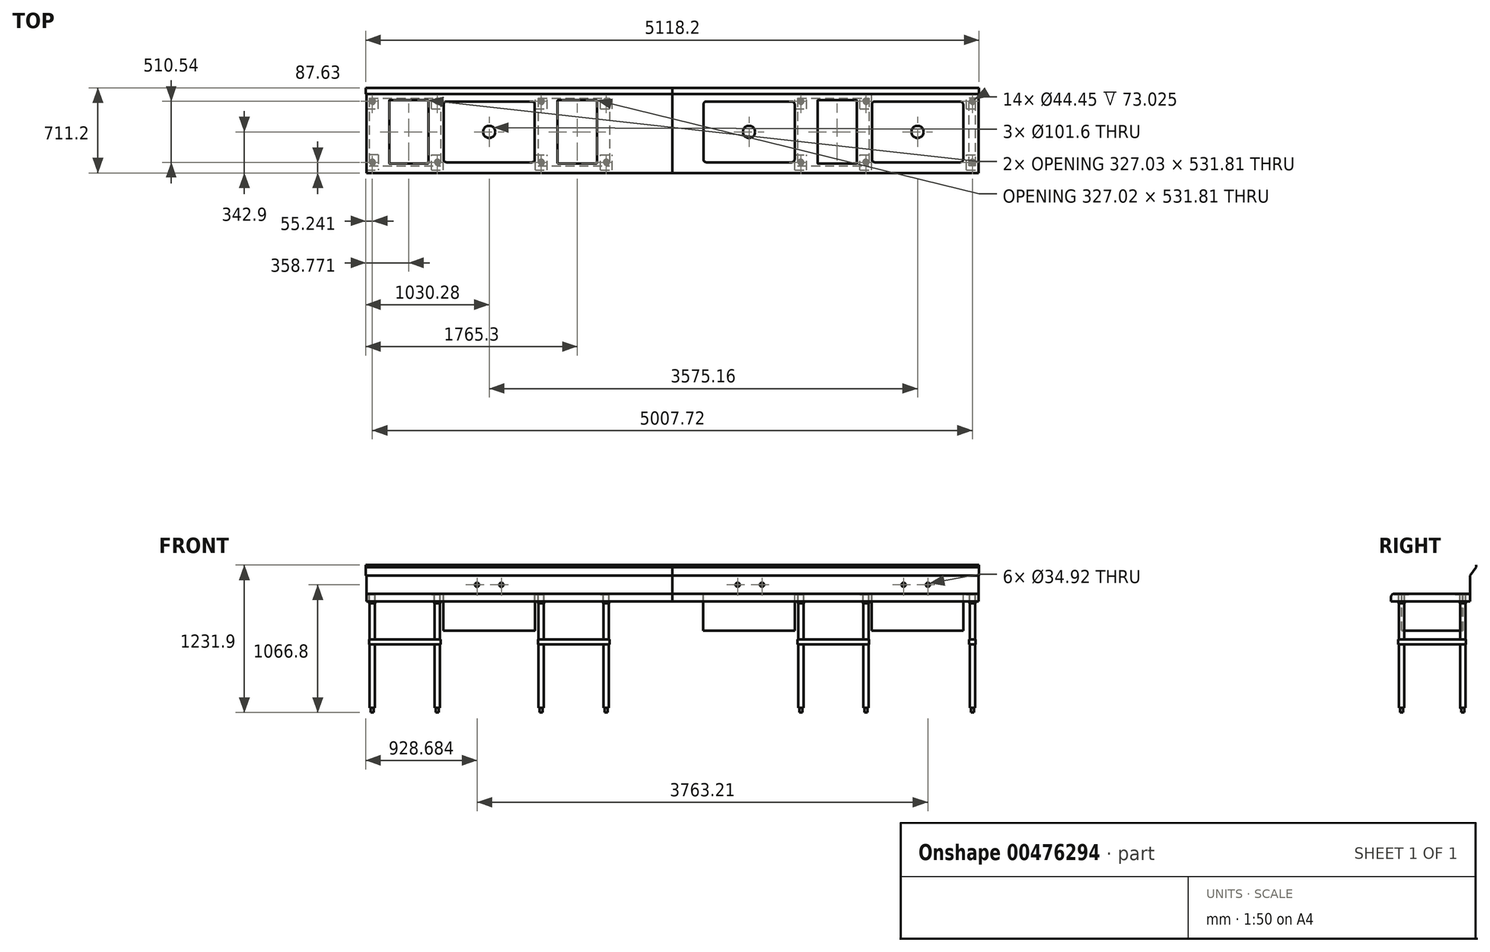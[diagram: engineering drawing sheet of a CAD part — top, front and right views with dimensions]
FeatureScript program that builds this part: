
annotation { "Feature Type Name" : "Feature", "Feature Type Description" : "" }
export const myFeature = defineFeature(function(context is Context, id is Id, definition is map)
    precondition{}
    {
        {
            var Q0;
            Q0=qCreatedBy(makeId("Top.planeOp"),FACE);
            var sketch = newSketch(context, id + "F0", { "sketchPlane" : qUnion([Q0])});
            skLineSegment(sketch, "E0.bottom", {"start": v(-2554.34, 342.9) * mm, "end": v(2554.34, 342.9) * mm});
            skLineSegment(sketch, "E0.top", {"start": v(-2554.34, -342.9) * mm, "end": v(2554.34, -342.9) * mm});
            skLineSegment(sketch, "E0.left", {"start": v(-2554.34, 342.9) * mm, "end": v(-2554.34, -342.9) * mm});
            skLineSegment(sketch, "E0.right", {"start": v(2554.34, 342.9) * mm, "end": v(2554.34, -342.9) * mm});
            skLineSegment(sketch, "E1", {"start": v(-2554.34, 0) * mm, "end": v(2554.34, 0) * mm, "construction": true});
            skLineSegment(sketch, "E2.bottom", {"start": v(-2363.84, 265.9) * mm, "end": v(-2036.82, 265.9) * mm, "construction": true});
            skLineSegment(sketch, "E2.top", {"start": v(-2363.84, -265.9) * mm, "end": v(-2036.82, -265.9) * mm, "construction": true});
            skLineSegment(sketch, "E2.left", {"start": v(-2363.84, 265.9) * mm, "end": v(-2363.84, -265.9) * mm, "construction": true});
            skLineSegment(sketch, "E2.right", {"start": v(-2036.82, 265.9) * mm, "end": v(-2036.82, -265.9) * mm, "construction": true});
            skLineSegment(sketch, "E3.bottom", {"start": v(-1909.82, 254) * mm, "end": v(-1147.82, 254) * mm, "construction": true});
            skLineSegment(sketch, "E3.top", {"start": v(-1909.82, -254) * mm, "end": v(-1147.82, -254) * mm, "construction": true});
            skLineSegment(sketch, "E3.left", {"start": v(-1909.82, 254) * mm, "end": v(-1909.82, -254) * mm, "construction": true});
            skLineSegment(sketch, "E3.right", {"start": v(-1147.82, 254) * mm, "end": v(-1147.82, -254) * mm, "construction": true});
            skLineSegment(sketch, "E4.bottom", {"start": v(-957.32, 265.9) * mm, "end": v(-630.3, 265.9) * mm, "construction": true});
            skLineSegment(sketch, "E4.top", {"start": v(-957.32, -265.9) * mm, "end": v(-630.3, -265.9) * mm, "construction": true});
            skLineSegment(sketch, "E4.left", {"start": v(-957.32, 265.9) * mm, "end": v(-957.32, -265.9) * mm, "construction": true});
            skLineSegment(sketch, "E4.right", {"start": v(-630.3, 265.9) * mm, "end": v(-630.3, -265.9) * mm, "construction": true});
            skLineSegment(sketch, "E5.bottom", {"start": v(258.82, 254) * mm, "end": v(1020.82, 254) * mm, "construction": true});
            skLineSegment(sketch, "E5.top", {"start": v(258.82, -254) * mm, "end": v(1020.82, -254) * mm, "construction": true});
            skLineSegment(sketch, "E5.left", {"start": v(258.82, 254) * mm, "end": v(258.82, -254) * mm, "construction": true});
            skLineSegment(sketch, "E5.right", {"start": v(1020.82, 254) * mm, "end": v(1020.82, -254) * mm, "construction": true});
            skLineSegment(sketch, "E6.bottom", {"start": v(1211.32, 265.9) * mm, "end": v(1538.34, 265.9) * mm, "construction": true});
            skLineSegment(sketch, "E6.top", {"start": v(1211.32, -265.9) * mm, "end": v(1538.34, -265.9) * mm, "construction": true});
            skLineSegment(sketch, "E6.left", {"start": v(1211.32, 265.9) * mm, "end": v(1211.32, -265.9) * mm, "construction": true});
            skLineSegment(sketch, "E6.right", {"start": v(1538.34, 265.9) * mm, "end": v(1538.34, -265.9) * mm, "construction": true});
            skLineSegment(sketch, "E7.bottom", {"start": v(1665.34, 254) * mm, "end": v(2427.34, 254) * mm, "construction": true});
            skLineSegment(sketch, "E7.top", {"start": v(1665.34, -254) * mm, "end": v(2427.34, -254) * mm, "construction": true});
            skLineSegment(sketch, "E7.left", {"start": v(1665.34, 254) * mm, "end": v(1665.34, -254) * mm, "construction": true});
            skLineSegment(sketch, "E7.right", {"start": v(2427.34, 254) * mm, "end": v(2427.34, -254) * mm, "construction": true});
            skLineSegment(sketch, "E8", {"start": v(-827.14, 342.9) * mm, "end": v(-827.14, -342.9) * mm, "construction": true});
            skLineSegment(sketch, "E9", {"start": v(900.06, 342.9) * mm, "end": v(900.06, -342.9) * mm, "construction": true});
            skLineSegment(sketch, "E10", {"start": v(-1528.82, 254) * mm, "end": v(-1528.82, -254) * mm, "construction": true});
            skPoint(sketch, "E11", {"position": v(-1528.82, 0) * mm});
            skPoint(sketch, "E12", {"position": v(-2363.84, 0) * mm});
            skSolve(sketch);
        }
        {
            var Q0;
            Q0 = qSketchRegion(id + "F0", true);
            extrude(context, id + "F1", {"entities" : qUnion([Q0]), "oppositeDirection" : true, "depth" : 304.93 * mm, "offsetDistance" : 25.4 * mm});
        }
        {
            var Q0;
            Q0=makeQuery(id+"F0.imprint","IMPRINT",FACE,{"disambiguationData":[TD([[makeQuery(id+"F0.imprint","IMPRINT",EDGE,{"derivedFrom":sQuery(id+"F0.wireOp",EDGE,"E0.bottom")}),-1.0]])]});
            var sketch = newSketch(context, id + "F2", { "sketchPlane" : qUnion([Q0])});
            skLineSegment(sketch, "E13.bottom", {"start": v(-1884.42, 254) * mm, "end": v(-1173.22, 254) * mm});
            skLineSegment(sketch, "E13.top", {"start": v(-1884.42, -254) * mm, "end": v(-1173.22, -254) * mm});
            skLineSegment(sketch, "E13.left", {"start": v(-1909.82, 228.6) * mm, "end": v(-1909.82, -228.6) * mm});
            skLineSegment(sketch, "E13.right", {"start": v(-1147.82, 228.6) * mm, "end": v(-1147.82, -228.6) * mm});
            skLineSegment(sketch, "E14.bottom", {"start": v(284.22, 254) * mm, "end": v(995.42, 254) * mm});
            skLineSegment(sketch, "E14.top", {"start": v(284.22, -254) * mm, "end": v(995.42, -254) * mm});
            skLineSegment(sketch, "E14.left", {"start": v(258.82, 228.6) * mm, "end": v(258.82, -228.6) * mm});
            skLineSegment(sketch, "E14.right", {"start": v(1020.82, 228.6) * mm, "end": v(1020.82, -228.6) * mm});
            skLineSegment(sketch, "E15.bottom", {"start": v(1690.74, 254) * mm, "end": v(2401.94, 254) * mm});
            skLineSegment(sketch, "E15.left", {"start": v(1665.34, 228.6) * mm, "end": v(1665.34, -228.6) * mm});
            skLineSegment(sketch, "E15.right", {"start": v(2427.34, 228.6) * mm, "end": v(2427.34, -228.6) * mm});
            skLineSegment(sketch, "E16", {"start": v(1690.74, -254) * mm, "end": v(2401.94, -254) * mm});
            skPoint(sketch, "E17.visualSharp", {"position": v(-1909.82, 254) * mm});
            skArc(sketch, "E17.filletArc", {"start": v(-1884.42, 254) * mm, "mid": v(-1902.38, 246.56) * mm, "end": v(-1909.82, 228.6) * mm});
            skPoint(sketch, "E18.visualSharp", {"position": v(-1909.82, -254) * mm});
            skArc(sketch, "E18.filletArc", {"start": v(-1909.82, -228.6) * mm, "mid": v(-1902.38, -246.56) * mm, "end": v(-1884.42, -254) * mm});
            skPoint(sketch, "E19.visualSharp", {"position": v(-1147.82, -254) * mm});
            skArc(sketch, "E19.filletArc", {"start": v(-1173.22, -254) * mm, "mid": v(-1155.26, -246.56) * mm, "end": v(-1147.82, -228.6) * mm});
            skPoint(sketch, "E20.visualSharp", {"position": v(-1147.82, 254) * mm});
            skArc(sketch, "E20.filletArc", {"start": v(-1147.82, 228.6) * mm, "mid": v(-1155.26, 246.56) * mm, "end": v(-1173.22, 254) * mm});
            skPoint(sketch, "E21.visualSharp", {"position": v(258.82, 254) * mm});
            skArc(sketch, "E21.filletArc", {"start": v(284.22, 254) * mm, "mid": v(266.26, 246.56) * mm, "end": v(258.82, 228.6) * mm});
            skPoint(sketch, "E22.visualSharp", {"position": v(258.82, -254) * mm});
            skArc(sketch, "E22.filletArc", {"start": v(258.82, -228.6) * mm, "mid": v(266.26, -246.56) * mm, "end": v(284.22, -254) * mm});
            skPoint(sketch, "E23.visualSharp", {"position": v(1020.82, 254) * mm});
            skArc(sketch, "E23.filletArc", {"start": v(1020.82, 228.6) * mm, "mid": v(1013.38, 246.56) * mm, "end": v(995.42, 254) * mm});
            skPoint(sketch, "E24.visualSharp", {"position": v(1020.82, -254) * mm});
            skArc(sketch, "E24.filletArc", {"start": v(995.42, -254) * mm, "mid": v(1013.38, -246.56) * mm, "end": v(1020.82, -228.6) * mm});
            skPoint(sketch, "E25.visualSharp", {"position": v(1665.34, 254) * mm});
            skArc(sketch, "E25.filletArc", {"start": v(1690.74, 254) * mm, "mid": v(1672.78, 246.56) * mm, "end": v(1665.34, 228.6) * mm});
            skPoint(sketch, "E26.visualSharp", {"position": v(2427.34, 254) * mm});
            skArc(sketch, "E26.filletArc", {"start": v(2427.34, 228.6) * mm, "mid": v(2419.9, 246.56) * mm, "end": v(2401.94, 254) * mm});
            skPoint(sketch, "E27.visualSharp", {"position": v(2427.34, -254) * mm});
            skArc(sketch, "E27.filletArc", {"start": v(2401.94, -254) * mm, "mid": v(2419.9, -246.56) * mm, "end": v(2427.34, -228.6) * mm});
            skPoint(sketch, "E28.visualSharp", {"position": v(1665.34, -254) * mm});
            skArc(sketch, "E28.filletArc", {"start": v(1665.34, -228.6) * mm, "mid": v(1672.78, -246.56) * mm, "end": v(1690.74, -254) * mm});
            skSolve(sketch);
        }
        {
            var Q0;
            Q0 = qSketchRegion(id + "F2", true);
            extrude(context, id + "F3", {"entities" : qUnion([Q0]), "operationType" : NewBodyOperationType.REMOVE, "oppositeDirection" : true, "depth" : 304.8 * mm, "offsetDistance" : 25.4 * mm});
        }
        {
            var Q0;
            Q0=makeQuery(id+"F1.opExtrude","CAP_EDGE",EDGE,{"disambiguationData":[OSD([sQuery(id+"F0.wireOp",EDGE,"E0.top")])],"isStart":true});
            fillet(context, id + "F4", {"entities" : qUnion([Q0]), "radius" : 25.4 * mm, "tangentPropagation" : true, "allowEdgeOverflow" : false});
        }
        {
            var Q0;
            Q0=makeQuery(id+"F1.opExtrude","CAP_FACE",FACE,{"disambiguationData":[OSD([sQuery(id+"F0.wireOp",EDGE,"E0.bottom"),sQuery(id+"F0.wireOp",EDGE,"E0.top"),sQuery(id+"F0.wireOp",EDGE,"E0.left"),sQuery(id+"F0.wireOp",EDGE,"E0.right")])],"isStart":false});
            shell(context, id + "F5", {"entities" : qUnion([Q0]), "thickness" : 1.27 * mm});
        }
        {
            var Q0;
            Q0=makeQuery(id+"F1.opExtrude","SWEPT_FACE",FACE,{"disambiguationData":[OSD([sQuery(id+"F0.wireOp",EDGE,"E0.bottom")])]});
            var sketch = newSketch(context, id + "F6", { "sketchPlane" : qUnion([Q0])});
            skLineSegment(sketch, "E29.bottom", {"start": v(-2554.34, 0) * mm, "end": v(2554.34, 0) * mm});
            skLineSegment(sketch, "E29.top", {"start": v(-2554.34, -304.93) * mm, "end": v(2554.34, -304.93) * mm});
            skLineSegment(sketch, "E29.left", {"start": v(-2554.34, 0) * mm, "end": v(-2554.34, -304.93) * mm});
            skLineSegment(sketch, "E29.right", {"start": v(2554.34, 0) * mm, "end": v(2554.34, -304.93) * mm});
            skSolve(sketch);
        }
        {
            var Q0;
            Q0 = qSketchRegion(id + "F6", true);
            extrude(context, id + "F7", {"entities" : qUnion([Q0]), "operationType" : NewBodyOperationType.REMOVE, "oppositeDirection" : true, "depth" : 25.4 * mm, "offsetDistance" : 25.4 * mm});
        }
        {
            var Q0;
            Q0=makeQuery(id+"F1.opExtrude","SWEPT_FACE",FACE,{"disambiguationData":[OSD([sQuery(id+"F0.wireOp",EDGE,"E0.top")])]});
            var sketch = newSketch(context, id + "F8", { "sketchPlane" : qUnion([Q0])});
            skLineSegment(sketch, "E30.bottom", {"start": v(-2554.34, -63.5) * mm, "end": v(2554.34, -63.5) * mm});
            skLineSegment(sketch, "E30.top", {"start": v(-2554.34, -304.93) * mm, "end": v(2554.34, -304.93) * mm});
            skLineSegment(sketch, "E30.left", {"start": v(-2554.34, -63.5) * mm, "end": v(-2554.34, -304.93) * mm});
            skLineSegment(sketch, "E30.right", {"start": v(2554.34, -63.5) * mm, "end": v(2554.34, -304.93) * mm});
            skSolve(sketch);
        }
        {
            var Q0;
            Q0 = qSketchRegion(id + "F8", true);
            extrude(context, id + "F9", {"entities" : qUnion([Q0]), "operationType" : NewBodyOperationType.REMOVE, "endBound" : BoundingType.UP_TO_NEXT, "oppositeDirection" : true, "depth" : 25.4 * mm, "offsetDistance" : 25.4 * mm});
        }
        {
            var Q0;
            Q0=makeQuery(id+"F1.opExtrude","CAP_FACE",FACE,{"disambiguationData":[OSD([sQuery(id+"F0.wireOp",EDGE,"E0.bottom"),sQuery(id+"F0.wireOp",EDGE,"E0.top"),sQuery(id+"F0.wireOp",EDGE,"E0.left"),sQuery(id+"F0.wireOp",EDGE,"E0.right")])],"isStart":true});
            var sketch = newSketch(context, id + "F10", { "sketchPlane" : qUnion([Q0])});
            skLineSegment(sketch, "E31.bottom", {"start": v(-2554.34, 316.23) * mm, "end": v(2554.34, 316.23) * mm});
            skLineSegment(sketch, "E31.top", {"start": v(-2554.34, 317.5) * mm, "end": v(2554.34, 317.5) * mm});
            skLineSegment(sketch, "E31.left", {"start": v(-2554.34, 316.23) * mm, "end": v(-2554.34, 317.5) * mm});
            skLineSegment(sketch, "E31.right", {"start": v(2554.34, 316.23) * mm, "end": v(2554.34, 317.5) * mm});
            skSolve(sketch);
        }
        {
            var Q0;
            Q0 = qSketchRegion(id + "F10", true);
            extrude(context, id + "F11", {"entities" : qUnion([Q0]), "operationType" : NewBodyOperationType.ADD, "depth" : 152.4 * mm, "offsetDistance" : 25.4 * mm});
        }
        {
            var Q0;
            Q0=makeQuery(id+"F1.opExtrude","CAP_FACE",FACE,{"disambiguationData":[OSD([sQuery(id+"F0.wireOp",EDGE,"E0.bottom"),sQuery(id+"F0.wireOp",EDGE,"E0.top"),sQuery(id+"F0.wireOp",EDGE,"E0.left"),sQuery(id+"F0.wireOp",EDGE,"E0.right")])],"isStart":true});
            var sketch = newSketch(context, id + "F12", { "sketchPlane" : qUnion([Q0])});
            skLineSegment(sketch, "E32.bottom", {"start": v(-2360.67, 265.9) * mm, "end": v(-2040, 265.9) * mm});
            skLineSegment(sketch, "E32.top", {"start": v(-2360.67, -265.9) * mm, "end": v(-2040, -265.9) * mm});
            skLineSegment(sketch, "E32.left", {"start": v(-2363.84, 262.73) * mm, "end": v(-2363.84, -262.73) * mm});
            skLineSegment(sketch, "E32.right", {"start": v(-2036.82, 262.73) * mm, "end": v(-2036.82, -262.73) * mm});
            skLineSegment(sketch, "E33.bottom", {"start": v(-954.14, 265.9) * mm, "end": v(-633.47, 265.9) * mm});
            skLineSegment(sketch, "E33.top", {"start": v(-954.14, -265.9) * mm, "end": v(-633.47, -265.9) * mm});
            skLineSegment(sketch, "E33.left", {"start": v(-957.32, 262.73) * mm, "end": v(-957.32, -262.73) * mm});
            skLineSegment(sketch, "E33.right", {"start": v(-630.3, 262.73) * mm, "end": v(-630.3, -262.73) * mm});
            skLineSegment(sketch, "E34.bottom", {"start": v(1214.5, 265.9) * mm, "end": v(1535.17, 265.9) * mm});
            skLineSegment(sketch, "E34.top", {"start": v(1214.5, -265.9) * mm, "end": v(1535.17, -265.9) * mm});
            skLineSegment(sketch, "E34.left", {"start": v(1211.32, 262.73) * mm, "end": v(1211.32, -262.73) * mm});
            skLineSegment(sketch, "E34.right", {"start": v(1538.34, 262.73) * mm, "end": v(1538.34, -262.73) * mm});
            skPoint(sketch, "E35.visualSharp", {"position": v(-2363.84, 265.9) * mm});
            skArc(sketch, "E35.filletArc", {"start": v(-2360.67, 265.9) * mm, "mid": v(-2362.91, 264.98) * mm, "end": v(-2363.84, 262.73) * mm});
            skPoint(sketch, "E36.visualSharp", {"position": v(-2036.82, 265.9) * mm});
            skArc(sketch, "E36.filletArc", {"start": v(-2036.82, 262.73) * mm, "mid": v(-2037.75, 264.98) * mm, "end": v(-2040, 265.9) * mm});
            skPoint(sketch, "E37.visualSharp", {"position": v(-2036.82, -265.9) * mm});
            skArc(sketch, "E37.filletArc", {"start": v(-2040, -265.9) * mm, "mid": v(-2037.75, -264.98) * mm, "end": v(-2036.82, -262.73) * mm});
            skPoint(sketch, "E38.visualSharp", {"position": v(-2363.84, -265.9) * mm});
            skArc(sketch, "E38.filletArc", {"start": v(-2363.84, -262.73) * mm, "mid": v(-2362.91, -264.98) * mm, "end": v(-2360.67, -265.9) * mm});
            skPoint(sketch, "E39.visualSharp", {"position": v(-957.32, -265.9) * mm});
            skArc(sketch, "E39.filletArc", {"start": v(-957.32, -262.73) * mm, "mid": v(-956.39, -264.98) * mm, "end": v(-954.14, -265.9) * mm});
            skPoint(sketch, "E40.visualSharp", {"position": v(-630.3, -265.9) * mm});
            skArc(sketch, "E40.filletArc", {"start": v(-633.47, -265.9) * mm, "mid": v(-631.22, -264.98) * mm, "end": v(-630.3, -262.73) * mm});
            skPoint(sketch, "E41.visualSharp", {"position": v(-630.3, 265.9) * mm});
            skArc(sketch, "E41.filletArc", {"start": v(-630.3, 262.73) * mm, "mid": v(-631.22, 264.98) * mm, "end": v(-633.47, 265.9) * mm});
            skPoint(sketch, "E42.visualSharp", {"position": v(-957.32, 265.9) * mm});
            skArc(sketch, "E42.filletArc", {"start": v(-954.14, 265.9) * mm, "mid": v(-956.39, 264.98) * mm, "end": v(-957.32, 262.73) * mm});
            skPoint(sketch, "E43.visualSharp", {"position": v(1211.32, 265.9) * mm});
            skArc(sketch, "E43.filletArc", {"start": v(1214.5, 265.9) * mm, "mid": v(1212.25, 264.98) * mm, "end": v(1211.32, 262.73) * mm});
            skPoint(sketch, "E44.visualSharp", {"position": v(1538.34, 265.9) * mm});
            skArc(sketch, "E44.filletArc", {"start": v(1538.34, 262.73) * mm, "mid": v(1537.41, 264.98) * mm, "end": v(1535.17, 265.9) * mm});
            skPoint(sketch, "E45.visualSharp", {"position": v(1538.34, -265.9) * mm});
            skArc(sketch, "E45.filletArc", {"start": v(1535.17, -265.9) * mm, "mid": v(1537.41, -264.98) * mm, "end": v(1538.34, -262.73) * mm});
            skPoint(sketch, "E46.visualSharp", {"position": v(1211.32, -265.9) * mm});
            skArc(sketch, "E46.filletArc", {"start": v(1211.32, -262.73) * mm, "mid": v(1212.25, -264.98) * mm, "end": v(1214.5, -265.9) * mm});
            skSolve(sketch);
        }
        {
            var Q0;
            Q0 = qSketchRegion(id + "F12", true);
            extrude(context, id + "F13", {"entities" : qUnion([Q0]), "operationType" : NewBodyOperationType.REMOVE, "endBound" : BoundingType.UP_TO_NEXT, "oppositeDirection" : true, "depth" : 25.4 * mm, "offsetDistance" : 25.4 * mm});
        }
        {
            var Q0;
            Q0=qCreatedBy(makeId("Right.planeOp"),FACE);
            var sketch = newSketch(context, id + "F14", { "sketchPlane" : qUnion([Q0])});
            skLineSegment(sketch, "E47", {"start": v(367.03, 222.25) * mm, "end": v(367.03, 241.3) * mm});
            skLineSegment(sketch, "E48", {"start": v(316.23, 152.4) * mm, "end": v(367.03, 222.25) * mm});
            skLineSegment(sketch, "E49", {"start": v(367.03, 222.25) * mm, "end": v(367.03, 152.4) * mm, "construction": true});
            skLineSegment(sketch, "E50.0", {"start": v(368.3, 222.25) * mm, "end": v(368.3, 241.3) * mm});
            skLineSegment(sketch, "E50.1", {"start": v(317.5, 152.4) * mm, "end": v(368.3, 222.25) * mm});
            skLineSegment(sketch, "E51", {"start": v(368.3, 241.3) * mm, "end": v(367.03, 241.3) * mm});
            skLineSegment(sketch, "E52", {"start": v(368.3, 222.25) * mm, "end": v(367.03, 222.25) * mm});
            skLineSegment(sketch, "E53", {"start": v(317.5, 152.4) * mm, "end": v(316.23, 152.4) * mm});
            skLineSegment(sketch, "E54", {"start": v(317.5, 152.4) * mm, "end": v(367.03, 152.4) * mm, "construction": true});
            skSolve(sketch);
        }
        {
            var Q0;
            Q0 = qSketchRegion(id + "F14", true);
            extrude(context, id + "F15", {"entities" : qUnion([Q0]), "operationType" : NewBodyOperationType.ADD, "endBound" : BoundingType.SYMMETRIC, "depth" : 5118.2 * mm, "offsetDistance" : 25.4 * mm});
        }
        {
            var Q0;
            Q0=makeQuery(id+"F5.opShell","OFFSET_FACE",FACE,{"disambiguationData":[OSD([sQuery(id+"F0.wireOp",EDGE,"E0.bottom"),sQuery(id+"F0.wireOp",EDGE,"E0.top"),sQuery(id+"F0.wireOp",EDGE,"E0.left"),sQuery(id+"F0.wireOp",EDGE,"E0.right")])]});
            var sketch = newSketch(context, id + "F16", { "sketchPlane" : qUnion([Q0])});
            skCircle(sketch, "E55", {"center": v(-2503.86, 255.27) * mm, "radius": 25.4 * mm});
            skCircle(sketch, "E56", {"center": v(-2503.86, -255.27) * mm, "radius": 25.4 * mm});
            skCircle(sketch, "E57", {"center": v(-1094.16, 255.27) * mm, "radius": 25.4 * mm});
            skCircle(sketch, "E58", {"center": v(-1094.16, -255.27) * mm, "radius": 25.4 * mm});
            skCircle(sketch, "E59", {"center": v(-551.23, 255.27) * mm, "radius": 25.4 * mm});
            skCircle(sketch, "E60", {"center": v(-551.23, -255.27) * mm, "radius": 25.4 * mm});
            skCircle(sketch, "E61", {"center": v(2503.86, -255.27) * mm, "radius": 25.4 * mm});
            skCircle(sketch, "E62", {"center": v(2503.86, 255.27) * mm, "radius": 25.4 * mm});
            skLineSegment(sketch, "E63.bottom", {"start": v(-2553.07, 317.5) * mm, "end": v(-2454.65, 317.5) * mm, "construction": true});
            skLineSegment(sketch, "E63.top", {"start": v(-2553.07, 193.04) * mm, "end": v(-2454.65, 193.04) * mm, "construction": true});
            skLineSegment(sketch, "E63.left", {"start": v(-2553.07, 317.5) * mm, "end": v(-2553.07, 193.04) * mm, "construction": true});
            skLineSegment(sketch, "E63.right", {"start": v(-2454.65, 317.5) * mm, "end": v(-2454.65, 193.04) * mm, "construction": true});
            skLineSegment(sketch, "E64.bottom", {"start": v(-2553.07, -317.5) * mm, "end": v(-2454.65, -317.5) * mm, "construction": true});
            skLineSegment(sketch, "E64.top", {"start": v(-2553.07, -193.04) * mm, "end": v(-2454.65, -193.04) * mm, "construction": true});
            skLineSegment(sketch, "E64.left", {"start": v(-2553.07, -317.5) * mm, "end": v(-2553.07, -193.04) * mm, "construction": true});
            skLineSegment(sketch, "E64.right", {"start": v(-2454.65, -317.5) * mm, "end": v(-2454.65, -193.04) * mm, "construction": true});
            skLineSegment(sketch, "E65.bottom", {"start": v(2553.07, -317.5) * mm, "end": v(2454.65, -317.5) * mm, "construction": true});
            skLineSegment(sketch, "E65.top", {"start": v(2553.07, -193.04) * mm, "end": v(2454.65, -193.04) * mm, "construction": true});
            skLineSegment(sketch, "E65.left", {"start": v(2553.07, -317.5) * mm, "end": v(2553.07, -193.04) * mm, "construction": true});
            skLineSegment(sketch, "E65.right", {"start": v(2454.65, -317.5) * mm, "end": v(2454.65, -193.04) * mm, "construction": true});
            skLineSegment(sketch, "E66.bottom", {"start": v(2553.07, 317.5) * mm, "end": v(2454.65, 317.5) * mm, "construction": true});
            skLineSegment(sketch, "E66.top", {"start": v(2553.07, 193.04) * mm, "end": v(2454.65, 193.04) * mm, "construction": true});
            skLineSegment(sketch, "E66.left", {"start": v(2553.07, 317.5) * mm, "end": v(2553.07, 193.04) * mm, "construction": true});
            skLineSegment(sketch, "E66.right", {"start": v(2454.65, 317.5) * mm, "end": v(2454.65, 193.04) * mm, "construction": true});
            skLineSegment(sketch, "E67.bottom", {"start": v(-600.45, 317.5) * mm, "end": v(-502.02, 317.5) * mm, "construction": true});
            skLineSegment(sketch, "E67.top", {"start": v(-600.45, 193.04) * mm, "end": v(-502.02, 193.04) * mm, "construction": true});
            skLineSegment(sketch, "E67.left", {"start": v(-600.45, 317.5) * mm, "end": v(-600.45, 193.04) * mm, "construction": true});
            skLineSegment(sketch, "E67.right", {"start": v(-502.02, 317.5) * mm, "end": v(-502.02, 193.04) * mm, "construction": true});
            skLineSegment(sketch, "E68.bottom", {"start": v(-600.45, -317.5) * mm, "end": v(-502.02, -317.5) * mm, "construction": true});
            skLineSegment(sketch, "E68.top", {"start": v(-600.45, -193.04) * mm, "end": v(-502.02, -193.04) * mm, "construction": true});
            skLineSegment(sketch, "E68.left", {"start": v(-600.45, -317.5) * mm, "end": v(-600.45, -193.04) * mm, "construction": true});
            skLineSegment(sketch, "E68.right", {"start": v(-502.02, -317.5) * mm, "end": v(-502.02, -193.04) * mm, "construction": true});
            skLineSegment(sketch, "E69.bottom", {"start": v(-1143.37, 317.5) * mm, "end": v(-1044.95, 317.5) * mm, "construction": true});
            skLineSegment(sketch, "E69.top", {"start": v(-1143.37, 193.04) * mm, "end": v(-1044.95, 193.04) * mm, "construction": true});
            skLineSegment(sketch, "E69.left", {"start": v(-1143.37, 317.5) * mm, "end": v(-1143.37, 193.04) * mm, "construction": true});
            skLineSegment(sketch, "E69.right", {"start": v(-1044.95, 317.5) * mm, "end": v(-1044.95, 193.04) * mm, "construction": true});
            skLineSegment(sketch, "E70.bottom", {"start": v(-1143.37, -317.5) * mm, "end": v(-1044.95, -317.5) * mm, "construction": true});
            skLineSegment(sketch, "E70.top", {"start": v(-1143.37, -193.04) * mm, "end": v(-1044.95, -193.04) * mm, "construction": true});
            skLineSegment(sketch, "E70.left", {"start": v(-1143.37, -317.5) * mm, "end": v(-1143.37, -193.04) * mm, "construction": true});
            skLineSegment(sketch, "E70.right", {"start": v(-1044.95, -317.5) * mm, "end": v(-1044.95, -193.04) * mm, "construction": true});
            skPoint(sketch, "E71", {"position": v(-2503.86, 317.5) * mm});
            skPoint(sketch, "E72", {"position": v(-2454.65, 255.27) * mm});
            skPoint(sketch, "E73", {"position": v(-2503.86, -193.04) * mm});
            skPoint(sketch, "E74", {"position": v(-2454.65, -255.27) * mm});
            skPoint(sketch, "E75", {"position": v(-1044.95, -255.27) * mm});
            skPoint(sketch, "E76", {"position": v(-1094.16, -317.5) * mm});
            skPoint(sketch, "E77", {"position": v(-1044.95, 255.27) * mm});
            skPoint(sketch, "E78", {"position": v(-1094.16, 193.04) * mm});
            skPoint(sketch, "E79", {"position": v(-502.02, 255.27) * mm});
            skPoint(sketch, "E80", {"position": v(-551.23, 193.04) * mm});
            skPoint(sketch, "E81", {"position": v(-502.02, -255.27) * mm});
            skPoint(sketch, "E82", {"position": v(-551.23, -193.04) * mm});
            skPoint(sketch, "E83", {"position": v(2553.07, -255.27) * mm});
            skPoint(sketch, "E84", {"position": v(2503.86, -317.5) * mm});
            skPoint(sketch, "E85", {"position": v(2553.07, 255.27) * mm});
            skPoint(sketch, "E86", {"position": v(2503.86, 193.04) * mm});
            skLineSegment(sketch, "E87.bottom", {"start": v(1022.72, -193.04) * mm, "end": v(1121.15, -193.04) * mm, "construction": true});
            skLineSegment(sketch, "E87.top", {"start": v(1022.72, -317.5) * mm, "end": v(1121.15, -317.5) * mm, "construction": true});
            skLineSegment(sketch, "E87.left", {"start": v(1022.72, -193.04) * mm, "end": v(1022.72, -317.5) * mm, "construction": true});
            skLineSegment(sketch, "E87.right", {"start": v(1121.15, -193.04) * mm, "end": v(1121.15, -317.5) * mm, "construction": true});
            skCircle(sketch, "E88", {"center": v(1071.93, -255.27) * mm, "radius": 25.4 * mm});
            skPoint(sketch, "E89", {"position": v(1071.93, -193.04) * mm});
            skPoint(sketch, "E90", {"position": v(1022.72, -255.27) * mm});
            skLineSegment(sketch, "E91.bottom", {"start": v(1022.72, 317.5) * mm, "end": v(1121.15, 317.5) * mm, "construction": true});
            skLineSegment(sketch, "E91.top", {"start": v(1022.72, 193.04) * mm, "end": v(1121.15, 193.04) * mm, "construction": true});
            skLineSegment(sketch, "E91.left", {"start": v(1022.72, 317.5) * mm, "end": v(1022.72, 193.04) * mm, "construction": true});
            skLineSegment(sketch, "E91.right", {"start": v(1121.15, 317.5) * mm, "end": v(1121.15, 193.04) * mm, "construction": true});
            skCircle(sketch, "E92", {"center": v(1071.93, 255.27) * mm, "radius": 25.4 * mm});
            skPoint(sketch, "E93", {"position": v(1022.72, 255.27) * mm});
            skPoint(sketch, "E94", {"position": v(1071.93, 317.5) * mm});
            skLineSegment(sketch, "E95.bottom", {"start": v(1565.65, 317.5) * mm, "end": v(1664.07, 317.5) * mm, "construction": true});
            skLineSegment(sketch, "E95.top", {"start": v(1565.65, 193.04) * mm, "end": v(1664.07, 193.04) * mm, "construction": true});
            skLineSegment(sketch, "E95.left", {"start": v(1565.65, 317.5) * mm, "end": v(1565.65, 193.04) * mm, "construction": true});
            skLineSegment(sketch, "E95.right", {"start": v(1664.07, 317.5) * mm, "end": v(1664.07, 193.04) * mm, "construction": true});
            skLineSegment(sketch, "E96.bottom", {"start": v(1565.65, -193.04) * mm, "end": v(1664.07, -193.04) * mm, "construction": true});
            skLineSegment(sketch, "E96.top", {"start": v(1565.65, -317.5) * mm, "end": v(1664.07, -317.5) * mm, "construction": true});
            skLineSegment(sketch, "E96.left", {"start": v(1565.65, -193.04) * mm, "end": v(1565.65, -317.5) * mm, "construction": true});
            skLineSegment(sketch, "E96.right", {"start": v(1664.07, -193.04) * mm, "end": v(1664.07, -317.5) * mm, "construction": true});
            skPoint(sketch, "E97.centerSnap0", {"position": v(1664.07, 255.27) * mm});
            skCircle(sketch, "E98", {"center": v(1614.86, 255.27) * mm, "radius": 25.4 * mm});
            skCircle(sketch, "E99", {"center": v(1614.86, -255.27) * mm, "radius": 25.4 * mm});
            skPoint(sketch, "E100", {"position": v(1565.65, 255.27) * mm});
            skPoint(sketch, "E101", {"position": v(1614.86, 317.5) * mm});
            skPoint(sketch, "E102", {"position": v(1565.65, -255.27) * mm});
            skPoint(sketch, "E103", {"position": v(1614.86, -193.04) * mm});
            skLineSegment(sketch, "E104.bottom", {"start": v(-2010.15, 317.5) * mm, "end": v(-1911.72, 317.5) * mm, "construction": true});
            skLineSegment(sketch, "E104.top", {"start": v(-2010.15, 193.04) * mm, "end": v(-1911.72, 193.04) * mm, "construction": true});
            skLineSegment(sketch, "E104.left", {"start": v(-2010.15, 317.5) * mm, "end": v(-2010.15, 193.04) * mm, "construction": true});
            skLineSegment(sketch, "E104.right", {"start": v(-1911.72, 317.5) * mm, "end": v(-1911.72, 193.04) * mm, "construction": true});
            skLineSegment(sketch, "E105.bottom", {"start": v(-2010.15, -193.04) * mm, "end": v(-1911.72, -193.04) * mm, "construction": true});
            skLineSegment(sketch, "E105.top", {"start": v(-2010.15, -317.5) * mm, "end": v(-1911.72, -317.5) * mm, "construction": true});
            skLineSegment(sketch, "E105.left", {"start": v(-2010.15, -193.04) * mm, "end": v(-2010.15, -317.5) * mm, "construction": true});
            skLineSegment(sketch, "E105.right", {"start": v(-1911.72, -193.04) * mm, "end": v(-1911.72, -317.5) * mm, "construction": true});
            skCircle(sketch, "E106", {"center": v(-1960.93, 255.27) * mm, "radius": 25.4 * mm});
            skPoint(sketch, "E106.centerSnap0", {"position": v(-2010.15, 255.27) * mm});
            skPoint(sketch, "E106.centerSnap1", {"position": v(-1960.93, 317.5) * mm});
            skCircle(sketch, "E107", {"center": v(-1960.93, -255.27) * mm, "radius": 25.4 * mm});
            skPoint(sketch, "E107.centerSnap0", {"position": v(-2010.15, -255.27) * mm});
            skPoint(sketch, "E107.centerSnap1", {"position": v(-1960.93, -193.04) * mm});
            skSolve(sketch);
        }
        {
            var Q0;
            Q0=makeQuery(id+"F1.opExtrude","CAP_FACE",FACE,{"disambiguationData":[OSD([sQuery(id+"F0.wireOp",EDGE,"E0.bottom"),sQuery(id+"F0.wireOp",EDGE,"E0.top"),sQuery(id+"F0.wireOp",EDGE,"E0.left"),sQuery(id+"F0.wireOp",EDGE,"E0.right")])],"isStart":true});
            cPlane(context, id + "F17", {"entities" : qUnion([Q0]), "cplaneType" : CPlaneType.OFFSET, "offset" : 381 * mm, "oppositeDirection" : true, "width" : 152.4 * mm, "height" : 152.4 * mm});
        }
        {
            var Q0;
            Q0 = qSketchRegion(id + "F16", true);
            extrude(context, id + "F18", {"entities" : qUnion([Q0]), "operationType" : NewBodyOperationType.ADD, "depth" : 76.2 * mm, "offsetDistance" : 25.4 * mm});
        }
        {
            var Q0;
            Q0=makeQuery(id+"F18.opExtrude","CAP_FACE",FACE,{"disambiguationData":[OSD([sQuery(id+"F16.wireOp",EDGE,"E62")])],"isStart":false});
            var Q1;
            Q1=makeQuery(id+"F18.opExtrude","CAP_FACE",FACE,{"disambiguationData":[OSD([sQuery(id+"F16.wireOp",EDGE,"E98")])],"isStart":false});
            var Q2;
            Q2=makeQuery(id+"F18.opExtrude","CAP_FACE",FACE,{"disambiguationData":[OSD([sQuery(id+"F16.wireOp",EDGE,"E99")])],"isStart":false});
            var Q3;
            Q3=makeQuery(id+"F18.opExtrude","CAP_FACE",FACE,{"disambiguationData":[OSD([sQuery(id+"F16.wireOp",EDGE,"E61")])],"isStart":false});
            var Q4;
            Q4=makeQuery(id+"F18.opExtrude","CAP_FACE",FACE,{"disambiguationData":[OSD([sQuery(id+"F16.wireOp",EDGE,"E88")])],"isStart":false});
            var Q5;
            Q5=makeQuery(id+"F18.opExtrude","CAP_FACE",FACE,{"disambiguationData":[OSD([sQuery(id+"F16.wireOp",EDGE,"E92")])],"isStart":false});
            var Q6;
            Q6=makeQuery(id+"F18.opExtrude","CAP_FACE",FACE,{"disambiguationData":[OSD([sQuery(id+"F16.wireOp",EDGE,"E59")])],"isStart":false});
            var Q7;
            Q7=makeQuery(id+"F18.opExtrude","CAP_FACE",FACE,{"disambiguationData":[OSD([sQuery(id+"F16.wireOp",EDGE,"E57")])],"isStart":false});
            var Q8;
            Q8=makeQuery(id+"F18.opExtrude","CAP_FACE",FACE,{"disambiguationData":[OSD([sQuery(id+"F16.wireOp",EDGE,"E58")])],"isStart":false});
            var Q9;
            Q9=makeQuery(id+"F18.opExtrude","CAP_FACE",FACE,{"disambiguationData":[OSD([sQuery(id+"F16.wireOp",EDGE,"E60")])],"isStart":false});
            var Q10;
            Q10=makeQuery(id+"F18.opExtrude","CAP_FACE",FACE,{"disambiguationData":[OSD([sQuery(id+"F16.wireOp",EDGE,"E106")])],"isStart":false});
            var Q11;
            Q11=makeQuery(id+"F18.opExtrude","CAP_FACE",FACE,{"disambiguationData":[OSD([sQuery(id+"F16.wireOp",EDGE,"E55")])],"isStart":false});
            var Q12;
            Q12=makeQuery(id+"F18.opExtrude","CAP_FACE",FACE,{"disambiguationData":[OSD([sQuery(id+"F16.wireOp",EDGE,"E56")])],"isStart":false});
            var Q13;
            Q13=makeQuery(id+"F18.opExtrude","CAP_FACE",FACE,{"disambiguationData":[OSD([sQuery(id+"F16.wireOp",EDGE,"E107")])],"isStart":false});
            shell(context, id + "F19", {"entities" : qUnion([Q0, Q1, Q2, Q3, Q4, Q5, Q6, Q7, Q8, Q9, Q10, Q11, Q12, Q13]), "thickness" : 3.17 * mm});
        }
        {
            var Q0;
            Q0=makeQuery(id+"F5.opShell","OFFSET_FACE",FACE,{"disambiguationData":[OSD([sQuery(id+"F0.wireOp",EDGE,"E0.bottom"),sQuery(id+"F0.wireOp",EDGE,"E0.top"),sQuery(id+"F0.wireOp",EDGE,"E0.left"),sQuery(id+"F0.wireOp",EDGE,"E0.right")])]});
            cPlane(context, id + "F20", {"entities" : qUnion([Q0]), "cplaneType" : CPlaneType.OFFSET, "offset" : 0 * mm, "width" : 152.4 * mm, "height" : 152.4 * mm});
        }
        {
            var Q0;
            Q0=qCreatedBy(id+"F20.planeOp",FACE);
            var sketch = newSketch(context, id + "F21", { "sketchPlane" : qUnion([Q0])});
            skLineSegment(sketch, "E108.bottom", {"start": v(-2454.65, 193.04) * mm, "end": v(-2553.07, 193.04) * mm});
            skLineSegment(sketch, "E108.top", {"start": v(-2454.65, 317.5) * mm, "end": v(-2553.07, 317.5) * mm});
            skLineSegment(sketch, "E108.left", {"start": v(-2454.65, 193.04) * mm, "end": v(-2454.65, 317.5) * mm});
            skLineSegment(sketch, "E108.right", {"start": v(-2553.07, 193.04) * mm, "end": v(-2553.07, 317.5) * mm});
            skLineSegment(sketch, "E109.bottom", {"start": v(-2010.15, 317.5) * mm, "end": v(-1911.72, 317.5) * mm});
            skLineSegment(sketch, "E109.top", {"start": v(-2010.15, 193.04) * mm, "end": v(-1911.72, 193.04) * mm});
            skLineSegment(sketch, "E109.left", {"start": v(-2010.15, 317.5) * mm, "end": v(-2010.15, 193.04) * mm});
            skLineSegment(sketch, "E109.right", {"start": v(-1911.72, 317.5) * mm, "end": v(-1911.72, 193.04) * mm});
            skLineSegment(sketch, "E110.bottom", {"start": v(-2553.07, -193.04) * mm, "end": v(-2454.65, -193.04) * mm});
            skLineSegment(sketch, "E110.top", {"start": v(-2553.07, -317.5) * mm, "end": v(-2454.65, -317.5) * mm});
            skLineSegment(sketch, "E110.left", {"start": v(-2553.07, -193.04) * mm, "end": v(-2553.07, -317.5) * mm});
            skLineSegment(sketch, "E110.right", {"start": v(-2454.65, -193.04) * mm, "end": v(-2454.65, -317.5) * mm});
            skLineSegment(sketch, "E111.bottom", {"start": v(-2010.15, -193.04) * mm, "end": v(-1911.72, -193.04) * mm});
            skLineSegment(sketch, "E111.top", {"start": v(-2010.15, -317.5) * mm, "end": v(-1911.72, -317.5) * mm});
            skLineSegment(sketch, "E111.left", {"start": v(-2010.15, -193.04) * mm, "end": v(-2010.15, -317.5) * mm});
            skLineSegment(sketch, "E111.right", {"start": v(-1911.72, -193.04) * mm, "end": v(-1911.72, -317.5) * mm});
            skLineSegment(sketch, "E112.bottom", {"start": v(-1143.37, -193.04) * mm, "end": v(-1044.95, -193.04) * mm});
            skLineSegment(sketch, "E112.top", {"start": v(-1143.37, -317.5) * mm, "end": v(-1044.95, -317.5) * mm});
            skLineSegment(sketch, "E112.left", {"start": v(-1143.37, -193.04) * mm, "end": v(-1143.37, -317.5) * mm});
            skLineSegment(sketch, "E112.right", {"start": v(-1044.95, -193.04) * mm, "end": v(-1044.95, -317.5) * mm});
            skLineSegment(sketch, "E113.bottom", {"start": v(-600.45, -193.04) * mm, "end": v(-502.02, -193.04) * mm});
            skLineSegment(sketch, "E113.top", {"start": v(-600.45, -317.5) * mm, "end": v(-502.02, -317.5) * mm});
            skLineSegment(sketch, "E113.left", {"start": v(-600.45, -193.04) * mm, "end": v(-600.45, -317.5) * mm});
            skLineSegment(sketch, "E113.right", {"start": v(-502.02, -193.04) * mm, "end": v(-502.02, -317.5) * mm});
            skLineSegment(sketch, "E114.bottom", {"start": v(-600.45, 317.5) * mm, "end": v(-502.02, 317.5) * mm});
            skLineSegment(sketch, "E114.top", {"start": v(-600.45, 193.04) * mm, "end": v(-502.02, 193.04) * mm});
            skLineSegment(sketch, "E114.left", {"start": v(-600.45, 317.5) * mm, "end": v(-600.45, 193.04) * mm});
            skLineSegment(sketch, "E114.right", {"start": v(-502.02, 317.5) * mm, "end": v(-502.02, 193.04) * mm});
            skLineSegment(sketch, "E115.bottom", {"start": v(-1143.37, 317.5) * mm, "end": v(-1044.95, 317.5) * mm});
            skLineSegment(sketch, "E115.top", {"start": v(-1143.37, 193.04) * mm, "end": v(-1044.95, 193.04) * mm});
            skLineSegment(sketch, "E115.left", {"start": v(-1143.37, 317.5) * mm, "end": v(-1143.37, 193.04) * mm});
            skLineSegment(sketch, "E115.right", {"start": v(-1044.95, 317.5) * mm, "end": v(-1044.95, 193.04) * mm});
            skLineSegment(sketch, "E116.bottom", {"start": v(1022.72, 317.5) * mm, "end": v(1121.15, 317.5) * mm});
            skLineSegment(sketch, "E116.top", {"start": v(1022.72, 193.04) * mm, "end": v(1121.15, 193.04) * mm});
            skLineSegment(sketch, "E116.left", {"start": v(1022.72, 317.5) * mm, "end": v(1022.72, 193.04) * mm});
            skLineSegment(sketch, "E116.right", {"start": v(1121.15, 317.5) * mm, "end": v(1121.15, 193.04) * mm});
            skLineSegment(sketch, "E117.bottom", {"start": v(1022.72, -193.04) * mm, "end": v(1121.15, -193.04) * mm});
            skLineSegment(sketch, "E117.top", {"start": v(1022.72, -317.5) * mm, "end": v(1121.15, -317.5) * mm});
            skLineSegment(sketch, "E117.left", {"start": v(1022.72, -193.04) * mm, "end": v(1022.72, -317.5) * mm});
            skLineSegment(sketch, "E117.right", {"start": v(1121.15, -193.04) * mm, "end": v(1121.15, -317.5) * mm});
            skLineSegment(sketch, "E118.bottom", {"start": v(1565.65, -193.04) * mm, "end": v(1664.07, -193.04) * mm});
            skLineSegment(sketch, "E118.top", {"start": v(1565.65, -317.5) * mm, "end": v(1664.07, -317.5) * mm});
            skLineSegment(sketch, "E118.left", {"start": v(1565.65, -193.04) * mm, "end": v(1565.65, -317.5) * mm});
            skLineSegment(sketch, "E118.right", {"start": v(1664.07, -193.04) * mm, "end": v(1664.07, -317.5) * mm});
            skLineSegment(sketch, "E119.bottom", {"start": v(1565.65, 317.5) * mm, "end": v(1664.07, 317.5) * mm});
            skLineSegment(sketch, "E119.top", {"start": v(1565.65, 193.04) * mm, "end": v(1664.07, 193.04) * mm});
            skLineSegment(sketch, "E119.left", {"start": v(1565.65, 317.5) * mm, "end": v(1565.65, 193.04) * mm});
            skLineSegment(sketch, "E119.right", {"start": v(1664.07, 317.5) * mm, "end": v(1664.07, 193.04) * mm});
            skLineSegment(sketch, "E120.bottom", {"start": v(2454.65, 317.5) * mm, "end": v(2553.07, 317.5) * mm});
            skLineSegment(sketch, "E120.top", {"start": v(2454.65, 193.04) * mm, "end": v(2553.07, 193.04) * mm});
            skLineSegment(sketch, "E120.left", {"start": v(2454.65, 317.5) * mm, "end": v(2454.65, 193.04) * mm});
            skLineSegment(sketch, "E120.right", {"start": v(2553.07, 317.5) * mm, "end": v(2553.07, 193.04) * mm});
            skLineSegment(sketch, "E121.bottom", {"start": v(2454.65, -193.04) * mm, "end": v(2553.07, -193.04) * mm});
            skLineSegment(sketch, "E121.top", {"start": v(2454.65, -317.5) * mm, "end": v(2553.07, -317.5) * mm});
            skLineSegment(sketch, "E121.left", {"start": v(2454.65, -193.04) * mm, "end": v(2454.65, -317.5) * mm});
            skLineSegment(sketch, "E121.right", {"start": v(2553.07, -193.04) * mm, "end": v(2553.07, -317.5) * mm});
            skSolve(sketch);
        }
        {
            var Q0;
            Q0 = qSketchRegion(id + "F21", true);
            extrude(context, id + "F22", {"entities" : qUnion([Q0]), "operationType" : NewBodyOperationType.ADD, "depth" : 3.17 * mm, "offsetDistance" : 25.4 * mm});
        }
        {
            var Q0;
            Q0=makeQuery(id+"F18.opExtrude","CAP_FACE",FACE,{"disambiguationData":[OSD([sQuery(id+"F16.wireOp",EDGE,"E59")])],"isStart":false});
            cPlane(context, id + "F23", {"entities" : qUnion([Q0]), "cplaneType" : CPlaneType.OFFSET, "offset" : 0 * mm, "width" : 152.4 * mm, "height" : 152.4 * mm});
        }
        {
            var Q0;
            Q0=qCreatedBy(id+"F23.planeOp",FACE);
            var sketch = newSketch(context, id + "F24", { "sketchPlane" : qUnion([Q0])});
            skCircle(sketch, "E122", {"center": v(-2503.86, 255.27) * mm, "radius": 22.35 * mm});
            skCircle(sketch, "E123", {"center": v(-1960.93, 255.27) * mm, "radius": 22.35 * mm});
            skCircle(sketch, "E124", {"center": v(-2503.86, -255.27) * mm, "radius": 22.35 * mm});
            skCircle(sketch, "E125", {"center": v(-1960.93, -255.27) * mm, "radius": 22.35 * mm});
            skCircle(sketch, "E126", {"center": v(-1094.16, -255.27) * mm, "radius": 22.35 * mm});
            skCircle(sketch, "E127", {"center": v(-551.23, -255.27) * mm, "radius": 22.35 * mm});
            skCircle(sketch, "E128", {"center": v(-551.23, 255.27) * mm, "radius": 22.35 * mm});
            skCircle(sketch, "E129", {"center": v(-1094.16, 255.27) * mm, "radius": 22.35 * mm});
            skCircle(sketch, "E130", {"center": v(1071.93, 255.27) * mm, "radius": 22.35 * mm});
            skCircle(sketch, "E131", {"center": v(1614.86, 255.27) * mm, "radius": 22.35 * mm});
            skCircle(sketch, "E132", {"center": v(1071.93, -255.27) * mm, "radius": 22.35 * mm});
            skCircle(sketch, "E133", {"center": v(1614.86, -255.27) * mm, "radius": 22.35 * mm});
            skCircle(sketch, "E134", {"center": v(2503.86, -255.27) * mm, "radius": 22.35 * mm});
            skCircle(sketch, "E135", {"center": v(2503.86, 255.27) * mm, "radius": 22.35 * mm});
            skSolve(sketch);
        }
        {
            var Q0;
            Q0 = qSketchRegion(id + "F24", true);
            extrude(context, id + "F25", {"entities" : qUnion([Q0]), "operationType" : NewBodyOperationType.ADD, "depth" : 875.03 * mm, "offsetDistance" : 25.4 * mm});
        }
        {
            var Q0;
            Q0=makeQuery(id+"F25.opExtrude","CAP_FACE",FACE,{"disambiguationData":[OSD([sQuery(id+"F24.wireOp",EDGE,"E122")])],"isStart":false});
            cPlane(context, id + "F26", {"entities" : qUnion([Q0]), "cplaneType" : CPlaneType.OFFSET, "offset" : 0 * mm, "width" : 152.4 * mm, "height" : 152.4 * mm});
        }
        {
            var Q0;
            Q0=qCreatedBy(id+"F26.planeOp",FACE);
            var sketch = newSketch(context, id + "F27", { "sketchPlane" : qUnion([Q0])});
            skCircle(sketch, "E136", {"center": v(-2503.86, 255.27) * mm, "radius": 12.7 * mm});
            skCircle(sketch, "E137", {"center": v(-1960.93, 255.27) * mm, "radius": 12.7 * mm});
            skCircle(sketch, "E138", {"center": v(-1094.16, 255.27) * mm, "radius": 12.7 * mm});
            skCircle(sketch, "E139", {"center": v(-551.23, 255.27) * mm, "radius": 12.7 * mm});
            skCircle(sketch, "E140", {"center": v(-2503.86, -255.27) * mm, "radius": 12.7 * mm});
            skCircle(sketch, "E141", {"center": v(-1960.93, -255.27) * mm, "radius": 12.7 * mm});
            skCircle(sketch, "E142", {"center": v(-1094.16, -255.27) * mm, "radius": 12.7 * mm});
            skCircle(sketch, "E143", {"center": v(-551.23, -255.27) * mm, "radius": 12.7 * mm});
            skCircle(sketch, "E144", {"center": v(1071.93, -255.27) * mm, "radius": 12.7 * mm});
            skCircle(sketch, "E145", {"center": v(1614.86, -255.27) * mm, "radius": 12.7 * mm});
            skCircle(sketch, "E146", {"center": v(1071.93, 255.27) * mm, "radius": 12.7 * mm});
            skCircle(sketch, "E147", {"center": v(1614.86, 255.27) * mm, "radius": 12.7 * mm});
            skCircle(sketch, "E148", {"center": v(2503.86, 255.27) * mm, "radius": 12.7 * mm});
            skCircle(sketch, "E149", {"center": v(2503.86, -255.27) * mm, "radius": 12.7 * mm});
            skSolve(sketch);
        }
        {
            var Q0;
            Q0 = qSketchRegion(id + "F27", true);
            extrude(context, id + "F28", {"entities" : qUnion([Q0]), "operationType" : NewBodyOperationType.ADD, "depth" : 38.1 * mm, "offsetDistance" : 25.4 * mm});
        }
        {
            var Q0;
            Q0=qCreatedBy(id+"F17.planeOp",FACE);
            var sketch = newSketch(context, id + "F29", { "sketchPlane" : qUnion([Q0])});
            skLineSegment(sketch, "E150.bottom", {"start": v(-2530.85, 282.26) * mm, "end": v(-1933.95, 282.26) * mm});
            skLineSegment(sketch, "E150.top", {"start": v(-2530.85, -282.26) * mm, "end": v(-1933.95, -282.26) * mm});
            skLineSegment(sketch, "E150.left", {"start": v(-2530.85, 282.26) * mm, "end": v(-2530.85, -282.26) * mm});
            skLineSegment(sketch, "E150.right", {"start": v(-1933.95, 282.26) * mm, "end": v(-1933.95, -282.26) * mm});
            skLineSegment(sketch, "E151.bottom", {"start": v(-1121.15, 282.26) * mm, "end": v(-524.25, 282.26) * mm});
            skLineSegment(sketch, "E151.top", {"start": v(-1121.15, -282.26) * mm, "end": v(-524.25, -282.26) * mm});
            skLineSegment(sketch, "E151.left", {"start": v(-1121.15, 282.26) * mm, "end": v(-1121.15, -282.26) * mm});
            skLineSegment(sketch, "E151.right", {"start": v(-524.25, 282.26) * mm, "end": v(-524.25, -282.26) * mm});
            skLineSegment(sketch, "E152.bottom", {"start": v(1044.95, 282.26) * mm, "end": v(1641.85, 282.26) * mm});
            skLineSegment(sketch, "E152.top", {"start": v(1044.95, -282.26) * mm, "end": v(1641.85, -282.26) * mm});
            skLineSegment(sketch, "E152.left", {"start": v(1044.95, 282.26) * mm, "end": v(1044.95, -282.26) * mm});
            skLineSegment(sketch, "E152.right", {"start": v(1641.85, 282.26) * mm, "end": v(1641.85, -282.26) * mm});
            skCircle(sketch, "E153", {"center": v(-2503.86, 255.27) * mm, "radius": 22.23 * mm});
            skCircle(sketch, "E154", {"center": v(-1960.93, 255.27) * mm, "radius": 22.23 * mm});
            skCircle(sketch, "E155", {"center": v(-2503.86, -255.27) * mm, "radius": 22.23 * mm});
            skCircle(sketch, "E156", {"center": v(-1960.93, -255.27) * mm, "radius": 22.23 * mm});
            skCircle(sketch, "E157", {"center": v(-1094.16, -255.27) * mm, "radius": 22.23 * mm});
            skCircle(sketch, "E158", {"center": v(-551.23, -255.27) * mm, "radius": 22.23 * mm});
            skCircle(sketch, "E159", {"center": v(-551.23, 255.27) * mm, "radius": 22.23 * mm});
            skCircle(sketch, "E160", {"center": v(-1094.16, 255.27) * mm, "radius": 22.23 * mm});
            skCircle(sketch, "E161", {"center": v(1071.93, 255.27) * mm, "radius": 22.23 * mm});
            skCircle(sketch, "E162", {"center": v(1071.93, -255.27) * mm, "radius": 22.23 * mm});
            skCircle(sketch, "E163", {"center": v(1614.86, -255.27) * mm, "radius": 22.23 * mm});
            skCircle(sketch, "E164", {"center": v(1614.86, 255.27) * mm, "radius": 22.23 * mm});
            skLineSegment(sketch, "E165", {"start": v(-2526.08, 255.27) * mm, "end": v(-1938.7, 255.27) * mm, "construction": true});
            skLineSegment(sketch, "E166", {"start": v(-2503.86, 277.5) * mm, "end": v(-2503.86, -277.5) * mm, "construction": true});
            skLineSegment(sketch, "E167.bottom", {"start": v(2530.85, -282.26) * mm, "end": v(2476.87, -282.26) * mm});
            skLineSegment(sketch, "E167.top", {"start": v(2530.85, 282.26) * mm, "end": v(2476.87, 282.26) * mm});
            skLineSegment(sketch, "E167.left", {"start": v(2530.85, -282.26) * mm, "end": v(2530.85, 282.26) * mm});
            skLineSegment(sketch, "E167.right", {"start": v(2476.87, -282.26) * mm, "end": v(2476.87, 282.26) * mm});
            skCircle(sketch, "E168", {"center": v(2503.86, 255.27) * mm, "radius": 22.23 * mm});
            skCircle(sketch, "E169", {"center": v(2503.86, -255.27) * mm, "radius": 22.23 * mm});
            skSolve(sketch);
        }
        {
            var Q0;
            Q0 = qSketchRegion(id + "F29", true);
            extrude(context, id + "F30", {"entities" : qUnion([Q0]), "operationType" : NewBodyOperationType.ADD, "oppositeDirection" : true, "depth" : 39.69 * mm, "offsetDistance" : 25.4 * mm});
        }
        {
            var Q0;
            Q0=qCreatedBy(makeId("Top.planeOp"),FACE);
            cPlane(context, id + "F31", {"entities" : qUnion([Q0]), "cplaneType" : CPlaneType.OFFSET, "offset" : 254 * mm, "width" : 152.4 * mm, "height" : 152.4 * mm});
        }
        {
            var Q0;
            Q0=qCreatedBy(id+"F31.planeOp",FACE);
            var sketch = newSketch(context, id + "F32", { "sketchPlane" : qUnion([Q0])});
            skLineSegment(sketch, "E170.bottom", {"start": v(-0.13, 367.03) * mm, "end": v(0.13, 367.03) * mm});
            skLineSegment(sketch, "E170.top", {"start": v(-0.13, -342.9) * mm, "end": v(0.13, -342.9) * mm});
            skLineSegment(sketch, "E170.left", {"start": v(-0.13, 367.03) * mm, "end": v(-0.13, -342.9) * mm});
            skLineSegment(sketch, "E170.right", {"start": v(0.13, 367.03) * mm, "end": v(0.13, -342.9) * mm});
            skLineSegment(sketch, "E171", {"start": v(0, 367.03) * mm, "end": v(0, -342.9) * mm, "construction": true});
            skSolve(sketch);
        }
        {
            var Q0;
            Q0 = qSketchRegion(id + "F32", true);
            extrude(context, id + "F33", {"entities" : qUnion([Q0]), "operationType" : NewBodyOperationType.REMOVE, "endBound" : BoundingType.THROUGH_ALL, "oppositeDirection" : true, "depth" : 25.4 * mm, "offsetDistance" : 25.4 * mm});
        }
        {
            var Q0;
            Q0=qCreatedBy(makeId("Top.planeOp"),FACE);
            var sketch = newSketch(context, id + "F34", { "sketchPlane" : qUnion([Q0])});
            skCircle(sketch, "E172", {"center": v(-1528.82, 0) * mm, "radius": 50.8 * mm});
            skCircle(sketch, "E173", {"center": v(639.82, 0) * mm, "radius": 50.8 * mm});
            skCircle(sketch, "E174", {"center": v(2046.34, 0) * mm, "radius": 50.8 * mm});
            skLineSegment(sketch, "E175", {"start": v(-1528.82, 254) * mm, "end": v(-1528.82, -254) * mm, "construction": true});
            skLineSegment(sketch, "E176", {"start": v(639.82, -254) * mm, "end": v(639.82, 254) * mm, "construction": true});
            skLineSegment(sketch, "E177", {"start": v(2046.34, 254) * mm, "end": v(2046.34, -254) * mm, "construction": true});
            skSolve(sketch);
        }
        {
            var Q0;
            Q0 = qSketchRegion(id + "F34", true);
            extrude(context, id + "F35", {"entities" : qUnion([Q0]), "operationType" : NewBodyOperationType.REMOVE, "endBound" : BoundingType.THROUGH_ALL, "oppositeDirection" : true, "depth" : 25.4 * mm, "offsetDistance" : 25.4 * mm});
        }
        {
            var Q0;
            {var subQ0=sQuery(id+"F0.wireOp",EDGE,"E0.left");Q0=makeQuery(id+"F33.boolean.opBoolean","SPLIT",FACE,{"disambiguationData":[TD([makeQuery(id+"F1.opExtrude","SWEPT_FACE",FACE,{"disambiguationData":[OSD([subQ0])]})])],"derivedFrom":makeQuery(id+"F11.opExtrude","SWEPT_FACE",FACE,{"disambiguationData":[OSD([sQuery(id+"F10.wireOp",EDGE,"E31.bottom")])]})});}
            var sketch = newSketch(context, id + "F36", { "sketchPlane" : qUnion([Q0])});
            skLineSegment(sketch, "E178", {"start": v(-2554.34, 76.2) * mm, "end": v(2554.34, 76.2) * mm, "construction": true});
            skLineSegment(sketch, "E179", {"start": v(-1528.82, -306.07) * mm, "end": v(-1528.82, 76.2) * mm, "construction": true});
            skLineSegment(sketch, "E180", {"start": v(639.82, -306.07) * mm, "end": v(639.82, 76.2) * mm, "construction": true});
            skLineSegment(sketch, "E181", {"start": v(2046.34, -306.07) * mm, "end": v(2046.34, 76.2) * mm, "construction": true});
            skCircle(sketch, "E182", {"center": v(-1630.42, 76.2) * mm, "radius": 17.46 * mm});
            skCircle(sketch, "E183", {"center": v(-1427.22, 76.2) * mm, "radius": 17.46 * mm});
            skCircle(sketch, "E184", {"center": v(545, 76.2) * mm, "radius": 17.46 * mm});
            skCircle(sketch, "E185", {"center": v(748.2, 76.2) * mm, "radius": 17.46 * mm});
            skCircle(sketch, "E186", {"center": v(2132.8, 76.2) * mm, "radius": 17.46 * mm});
            skCircle(sketch, "E187", {"center": v(1929.6, 76.2) * mm, "radius": 17.46 * mm});
            skSolve(sketch);
        }
        {
            var Q0;
            Q0 = qSketchRegion(id + "F36", true);
            extrude(context, id + "F37", {"entities" : qUnion([Q0]), "operationType" : NewBodyOperationType.REMOVE, "oppositeDirection" : true, "depth" : 25.4 * mm, "offsetDistance" : 25.4 * mm});
        }
    });
